# Revit family: Sling_CB-571_BIM
name_source: partatom
category: Arredi
units: mm (PartAtom-declared; Revit-internal decimal feet)

## family parameters
Attiva taglio nelle viste = No
Basato su piano di lavoro = No
Condiviso = No
Numero OmniClass = 23.40.20.00
Origine composizione di rendering = Geometria famiglia
Punto di calcolo locali = No
Sempre verticale = Sì
Taglio con vuoti quando caricato = No
Titolo OmniClass = General Furniture and Specialties

## types (1)
- CB-571
    AVAILABLE FINISHES = Ebonized black lacquer on Ash (EB) or bleached, white pigment, matte acrylic on Ash (BL). Raw effect lacquer on Oak (RE). Hand rubbed natural oil on Oak or Walnut (NA), or hand rubbed black oil on Walnut (BO). Frame: satin nickel (SN), satin brass (SB), bronze (BZ) or gunmetal (GM) nanoceramic coating. Suspension: Vachetta (VB), Brown (BB), Black (NB).
    BASE MATERIAL = BASSAM_FELLOWS_COMFORT_LEATHER_43632_CAMEL
    BIM BADGE = https://bim.archiproducts.com
    COLLECTION = Sling
    DEPTH = 570 mm
    Descrizione = Leather, wood and steel ottoman
    HEIGHT = 464 mm
    MATERIAL DESCRIPTION = Solid wood posts with tubular steel crossbeams. Upholstery: Feather and down cushions. Double topstitch detail. Suspension: Double layer belting leather.
    Modello = Sling Ottoman
    PRODUCT CODE = CB-571
    PRODUCT SHEET = https://www.archiproducts.com
    Produttore = BassamFellows
    Prospetto di default = 0 mm  [stored 0 ft]
    STRUCTURE MATERIAL = BASSAM_FELLOWS_WALNUT_BLACK_OIL_W-BO
    TECHNICAL SHEET = https://bassamfellows.com
    URL = https://bassamfellows.com
    WIDTH = 775 mm

note: [stored X ft] marks values corroborated as IEEE doubles in the binary element streams (Revit-internal decimal feet)

## geometry (parser evidence)
native form markers: Sweep x2
no freeform markers — native parametric forms only
